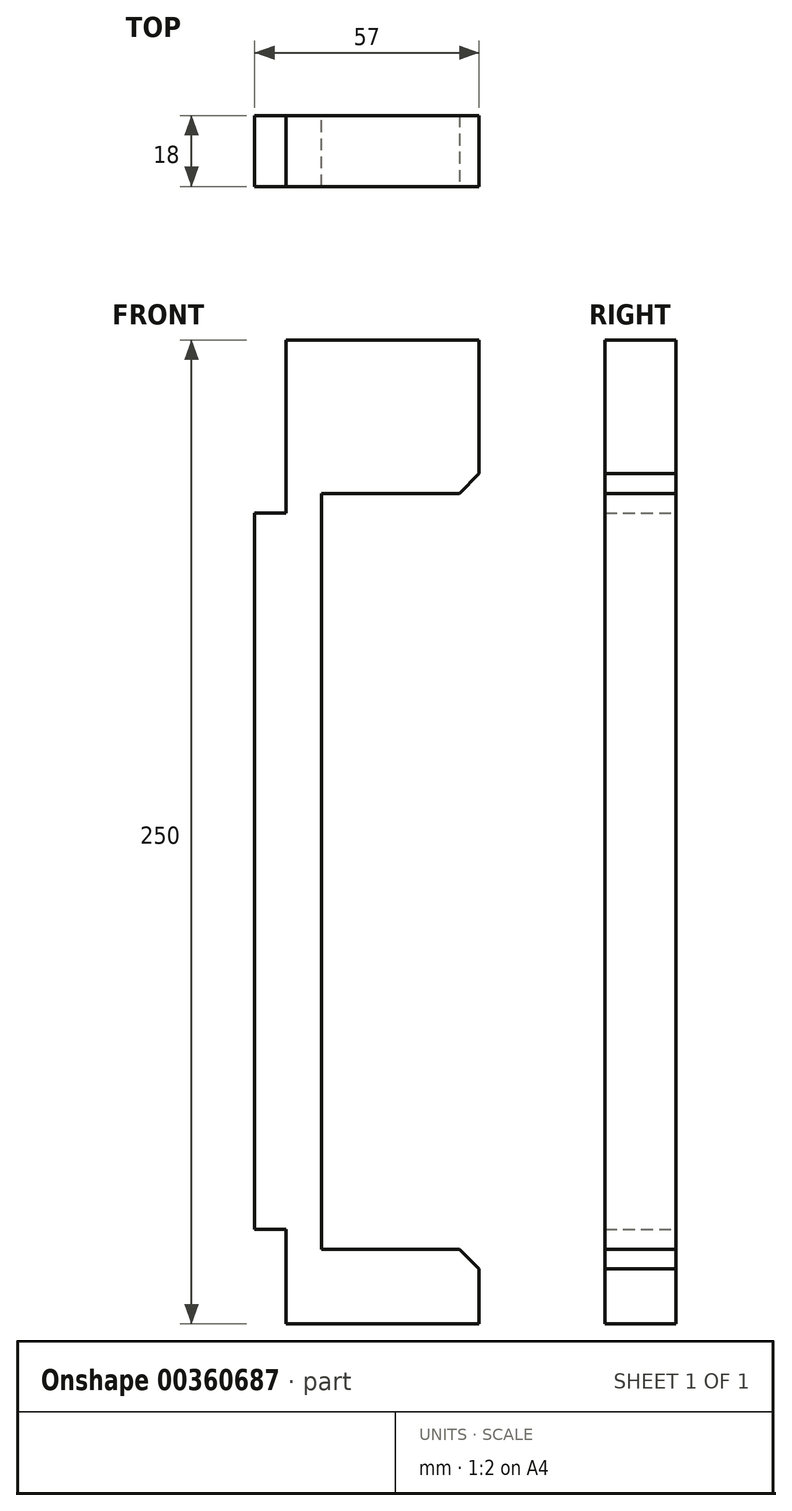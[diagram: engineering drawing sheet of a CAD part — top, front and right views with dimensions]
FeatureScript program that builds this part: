
annotation { "Feature Type Name" : "Feature", "Feature Type Description" : "" }
export const myFeature = defineFeature(function(context is Context, id is Id, definition is map)
    precondition{}
    {
        {
            var Q0;
            Q0=qCreatedBy(makeId("Front.planeOp"),FACE);
            var sketch = newSketch(context, id + "F0", { "sketchPlane" : qUnion([Q0])});
            skLineSegment(sketch, "E0.bottom", {"start": v(0, 0) * mm, "end": v(49, 0) * mm});
            skLineSegment(sketch, "E0.top", {"start": v(9, 19) * mm, "end": v(49, 19) * mm});
            skLineSegment(sketch, "E0.right", {"start": v(49, 0) * mm, "end": v(49, 19) * mm});
            skLineSegment(sketch, "E1.bottom", {"start": v(0, 250) * mm, "end": v(49, 250) * mm});
            skLineSegment(sketch, "E1.top", {"start": v(9, 211) * mm, "end": v(49, 211) * mm});
            skLineSegment(sketch, "E1.right", {"start": v(49, 250) * mm, "end": v(49, 211) * mm});
            skLineSegment(sketch, "E2", {"start": v(9, 211) * mm, "end": v(9, 19) * mm});
            skLineSegment(sketch, "E3", {"start": v(0, 250) * mm, "end": v(0, 206) * mm});
            skLineSegment(sketch, "E4.bottom", {"start": v(-8, 206) * mm, "end": v(0, 206) * mm});
            skLineSegment(sketch, "E4.top", {"start": v(-8, 24) * mm, "end": v(0, 24) * mm});
            skLineSegment(sketch, "E4.left", {"start": v(-8, 206) * mm, "end": v(-8, 24) * mm});
            skLineSegment(sketch, "E5.trimOffspring", {"start": v(0, 24) * mm, "end": v(0, 0) * mm});
            skSolve(sketch);
        }
        {
            var Q0;
            Q0=makeQuery(id+"F0.imprint","IMPRINT",FACE,{"disambiguationData":[TD([[makeQuery(id+"F0.imprint","IMPRINT",EDGE,{"derivedFrom":sQuery(id+"F0.wireOp",EDGE,"E0.bottom")}),1.0]])]});
            extrude(context, id + "F1", {"entities" : qUnion([Q0]), "depth" : 18 * mm});
        }
        {
            var Q0;
            Q0=makeQuery(id+"F1.opExtrude","SWEPT_EDGE",EDGE,{"disambiguationData":[OSD([sQuery(id+"F0.wireOp",EDGE,"E1.top"),sQuery(id+"F0.wireOp",EDGE,"E1.right")])]});
            var Q1;
            Q1=makeQuery(id+"F1.opExtrude","SWEPT_EDGE",EDGE,{"disambiguationData":[OSD([sQuery(id+"F0.wireOp",EDGE,"E0.top"),sQuery(id+"F0.wireOp",EDGE,"E0.right")])]});
            chamfer(context, id + "F2", {"entities" : qUnion([Q0, Q1]), "width" : 5 * mm, "tangentPropagation" : true});
        }
    });
